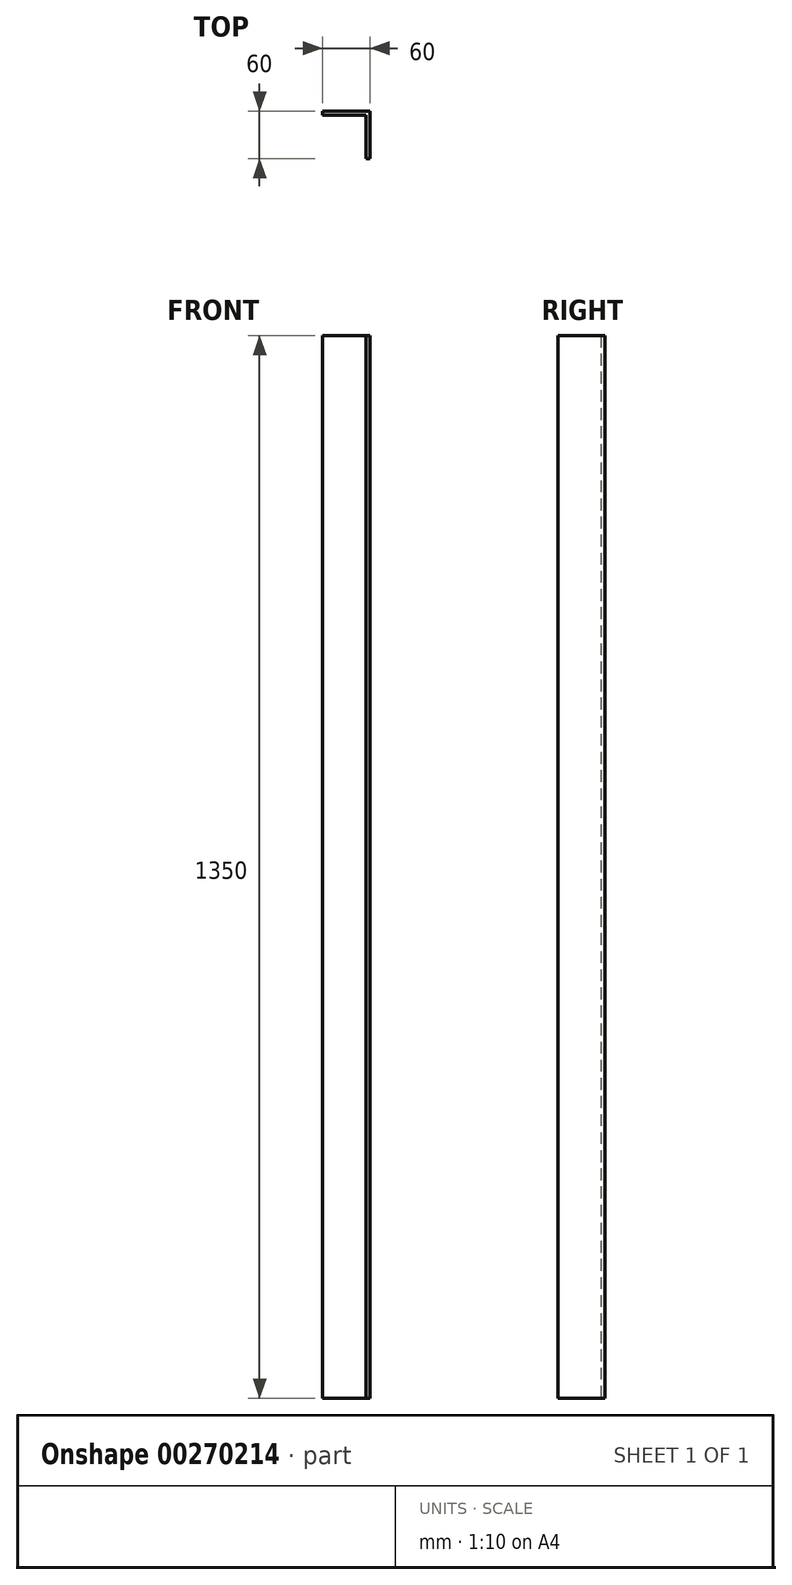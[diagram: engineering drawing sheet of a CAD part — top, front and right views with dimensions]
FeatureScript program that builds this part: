
annotation { "Feature Type Name" : "Feature", "Feature Type Description" : "" }
export const myFeature = defineFeature(function(context is Context, id is Id, definition is map)
    precondition{}
    {
        {
            var Q0;
            Q0=qCreatedBy(makeId("Top.planeOp"),FACE);
            var sketch = newSketch(context, id + "F0", { "sketchPlane" : qUnion([Q0])});
            skLineSegment(sketch, "E0", {"start": v(-33.03, 28.7) * mm, "end": v(26.97, 28.7) * mm});
            skLineSegment(sketch, "E1", {"start": v(26.97, 28.7) * mm, "end": v(26.97, -31.3) * mm});
            skLineSegment(sketch, "E2", {"start": v(26.97, -31.3) * mm, "end": v(21.97, -31.3) * mm});
            skLineSegment(sketch, "E3", {"start": v(21.97, -31.3) * mm, "end": v(21.97, 23.7) * mm});
            skLineSegment(sketch, "E4", {"start": v(21.97, 23.7) * mm, "end": v(-33.03, 23.7) * mm});
            skLineSegment(sketch, "E5", {"start": v(-33.03, 23.7) * mm, "end": v(-33.03, 28.7) * mm});
            skSolve(sketch);
        }
        {
            var Q0;
            Q0=makeQuery(id+"F0.imprint","IMPRINT",FACE,{"disambiguationData":[TD([[makeQuery(id+"F0.imprint","IMPRINT",EDGE,{"derivedFrom":sQuery(id+"F0.wireOp",EDGE,"E0")}),-1.0]])]});
            extrude(context, id + "F1", {"entities" : qUnion([Q0]), "depth" : 1350 * mm});
        }
    });
